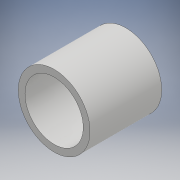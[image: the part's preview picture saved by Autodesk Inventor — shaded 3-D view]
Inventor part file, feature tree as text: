
AUTODESK INVENTOR PART (.ipt)
format: ipt  version: 2018 (Build 220112000, 112)  size: 98,816 bytes
history: native  units: mm
features: extrude x1, sketch x1
ambient origin geometry x8: Origin, YZ Plane, XZ Plane, XY Plane, X Axis, Y Axis, Z Axis, Center Point
bodies: Solid1 (feature_tree)
feature tree (2):
  extrude  "Extrusion1"  Depth=4.0mm
  sketch  "Sketch1"  dims[d0=4.0mm d1=3.25mm d2=4.0mm d3=0.0mm]
